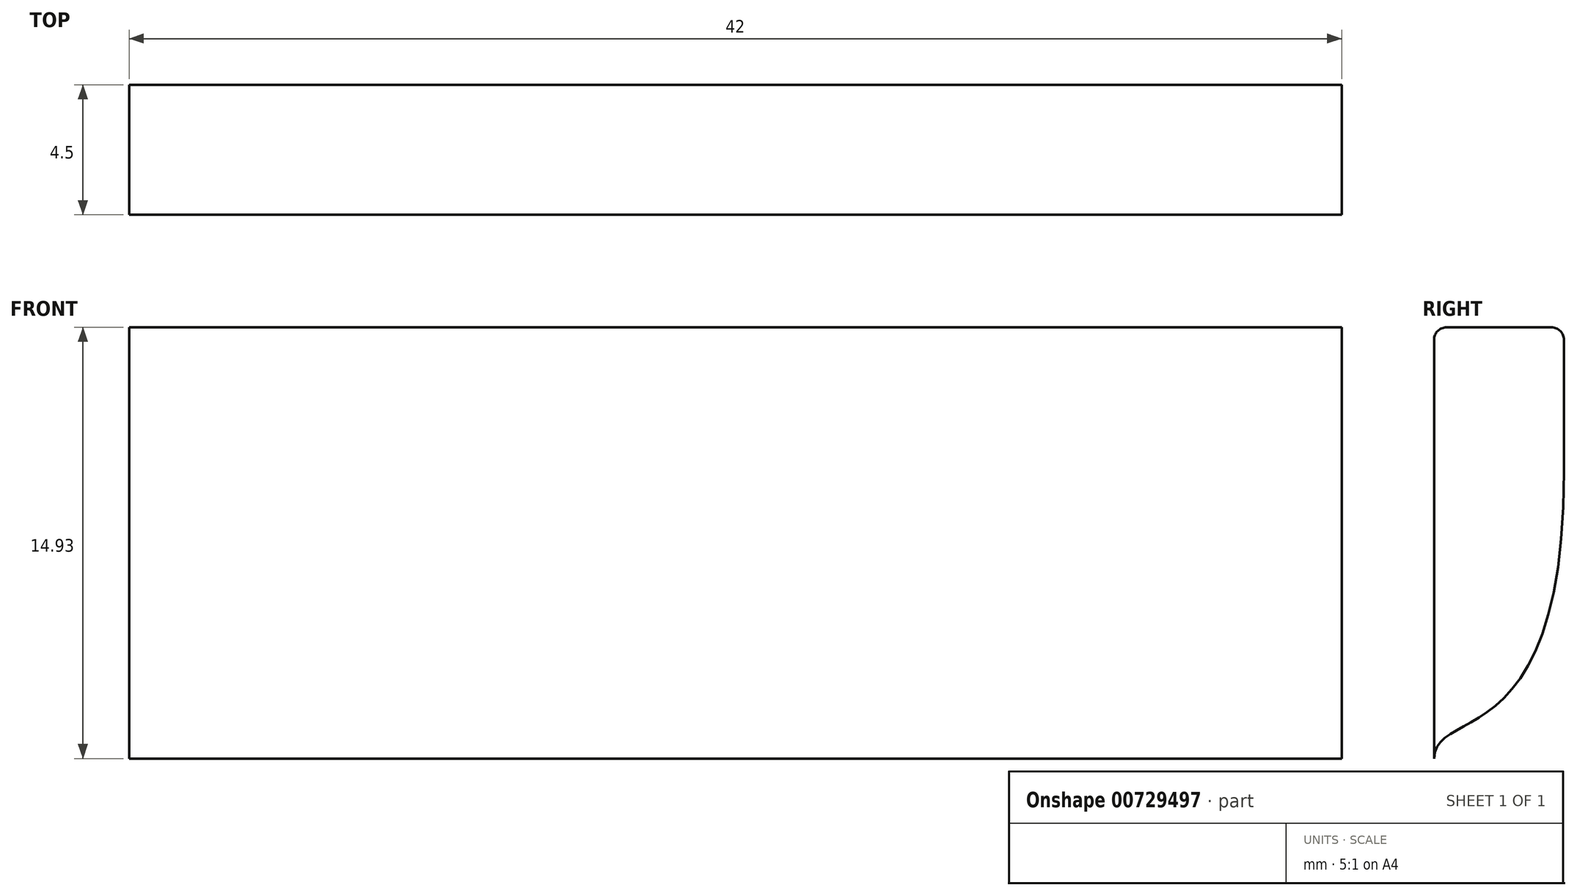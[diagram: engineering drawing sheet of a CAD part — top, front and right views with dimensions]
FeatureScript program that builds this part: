
annotation { "Feature Type Name" : "Feature", "Feature Type Description" : "" }
export const myFeature = defineFeature(function(context is Context, id is Id, definition is map)
    precondition{}
    {
        {
            var Q0;
            Q0=qCreatedBy(makeId("Right.planeOp"),FACE);
            var sketch = newSketch(context, id + "F0", { "sketchPlane" : qUnion([Q0])});
            skLineSegment(sketch, "E0.bottom", {"start": v(-2.25, -10) * mm, "end": v(2.25, -10) * mm});
            skLineSegment(sketch, "E0.top", {"start": v(-2.25, 10) * mm, "end": v(2.25, 10) * mm});
            skLineSegment(sketch, "E0.left", {"start": v(-2.25, -9.57) * mm, "end": v(-2.25, 10) * mm});
            skLineSegment(sketch, "E0.right", {"start": v(2.25, -10) * mm, "end": v(2.25, 10) * mm});
            skPoint(sketch, "E0.middle", {"position": v(0, 0) * mm});
            skLineSegment(sketch, "E1", {"start": v(1.82, -10) * mm, "end": v(-1.82, -10) * mm});
            skLineSegment(sketch, "E2", {"start": v(2.25, -9.57) * mm, "end": v(2.25, 10) * mm});
            skLineSegment(sketch, "E3", {"start": v(0, 10) * mm, "end": v(-6.75, 10) * mm});
            skFitSpline(sketch, "E4", {"points": [v(-2.25, 0) * mm, v(-6.75, 10) * mm], "startDerivative": vector(0.16, 5.93) * mm, "endDerivative": vector(-0.01, 30) * mm});
            skFitSpline(sketch, "E5.MirrorCS", {"points": [v(2.25, 0) * mm, v(6.75, 10) * mm], "startDerivative": vector(-0.16, 5.93) * mm, "endDerivative": vector(0.01, 30) * mm});
            skLineSegment(sketch, "E6.MirrorCS", {"start": v(0, 10) * mm, "end": v(6.75, 10) * mm});
            skLineSegment(sketch, "E7.bottom", {"start": v(2.25, 10) * mm, "end": v(-2.25, 10) * mm});
            skLineSegment(sketch, "E7.top", {"start": v(2.25, 5.78) * mm, "end": v(-2.25, 5.78) * mm});
            skLineSegment(sketch, "E7.left", {"start": v(2.25, 10) * mm, "end": v(2.25, 5.78) * mm});
            skLineSegment(sketch, "E7.right", {"start": v(-2.25, 10) * mm, "end": v(-2.25, 5.78) * mm});
            skLineSegment(sketch, "E8.bottom", {"start": v(-2.25, 10) * mm, "end": v(-6.75, 10) * mm});
            skLineSegment(sketch, "E8.top", {"start": v(-2.68, 15) * mm, "end": v(-6.32, 15) * mm});
            skLineSegment(sketch, "E8.left", {"start": v(-2.25, 10) * mm, "end": v(-2.25, 14.57) * mm});
            skLineSegment(sketch, "E8.right", {"start": v(-6.75, 10) * mm, "end": v(-6.75, 15) * mm});
            skLineSegment(sketch, "E9", {"start": v(-6.75, 14.57) * mm, "end": v(-6.75, 10) * mm});
            skLineSegment(sketch, "E10.MirrorCS", {"start": v(6.75, 14.57) * mm, "end": v(6.75, 10) * mm});
            skLineSegment(sketch, "E11.MirrorCS", {"start": v(2.25, 10) * mm, "end": v(2.25, 14.57) * mm});
            skLineSegment(sketch, "E12.MirrorCS", {"start": v(2.68, 15) * mm, "end": v(6.32, 15) * mm});
            skPoint(sketch, "E13.visualSharp", {"position": v(6.75, 15) * mm});
            skArc(sketch, "E13.filletArc", {"start": v(6.75, 14.57) * mm, "mid": v(6.62, 14.87) * mm, "end": v(6.32, 15) * mm});
            skPoint(sketch, "E14.visualSharp", {"position": v(2.25, 15) * mm});
            skArc(sketch, "E14.filletArc", {"start": v(2.68, 15) * mm, "mid": v(2.38, 14.87) * mm, "end": v(2.25, 14.57) * mm});
            skPoint(sketch, "E15.visualSharp", {"position": v(-2.25, 15) * mm});
            skArc(sketch, "E15.filletArc", {"start": v(-2.25, 14.57) * mm, "mid": v(-2.38, 14.87) * mm, "end": v(-2.68, 15) * mm});
            skPoint(sketch, "E16.visualSharp", {"position": v(-6.75, 15) * mm});
            skArc(sketch, "E16.filletArc", {"start": v(-6.32, 15) * mm, "mid": v(-6.62, 14.87) * mm, "end": v(-6.75, 14.57) * mm});
            skPoint(sketch, "E17.visualSharp", {"position": v(2.25, -10) * mm});
            skArc(sketch, "E17.filletArc", {"start": v(1.82, -10) * mm, "mid": v(2.12, -9.87) * mm, "end": v(2.25, -9.57) * mm});
            skPoint(sketch, "E18.visualSharp", {"position": v(-2.25, -10) * mm});
            skArc(sketch, "E18.filletArc", {"start": v(-2.25, -9.57) * mm, "mid": v(-2.12, -9.87) * mm, "end": v(-1.82, -10) * mm});
            skSolve(sketch);
        }
        {
            var Q0;
            Q0=makeQuery(id+"F0.imprint","IMPRINT",FACE,{"disambiguationData":[TD([[makeQuery(id+"F0.imprint","IMPRINT",EDGE,{"derivedFrom":sQuery(id+"F0.wireOp",EDGE,"E6.MirrorCS")}),1.0]])]});
            var Q1;
            {var subQ4=sQuery(id+"F0.wireOp",EDGE,"E6.MirrorCS");Q1=makeQuery(id+"F0.imprint","IMPRINT",FACE,{"disambiguationData":[TD([[makeQuery(id+"F0.imprint","IMPRINT",EDGE,{"derivedFrom":subQ4}),-1.0]])]});}
            var Q2;
            Q2=makeQuery(id+"F0.imprint","IMPRINT",FACE,{"disambiguationData":[TD([[makeQuery(id+"F0.imprint","IMPRINT",EDGE,{"derivedFrom":sQuery(id+"F0.wireOp",EDGE,"E1")}),-1.0]])]});
            var Q3;
            {var subQ0=sQuery(id+"F0.wireOp",EDGE,"E7.right");Q3=makeQuery(id+"F0.imprint","IMPRINT",FACE,{"disambiguationData":[TD([[makeQuery(id+"F0.imprint","IMPRINT",EDGE,{"derivedFrom":subQ0}),-1.0]])]});}
            var Q4;
            Q4=makeQuery(id+"F0.imprint","IMPRINT",FACE,{"disambiguationData":[TD([[makeQuery(id+"F0.imprint","IMPRINT",EDGE,{"derivedFrom":sQuery(id+"F0.wireOp",EDGE,"E8.bottom")}),-1.0]])]});
            extrude(context, id + "F1", {"entities" : qUnion([Q0, Q1, Q2, Q3, Q4]), "depth" : 42 * mm, "offsetDistance" : 25 * mm});
        }
    });
